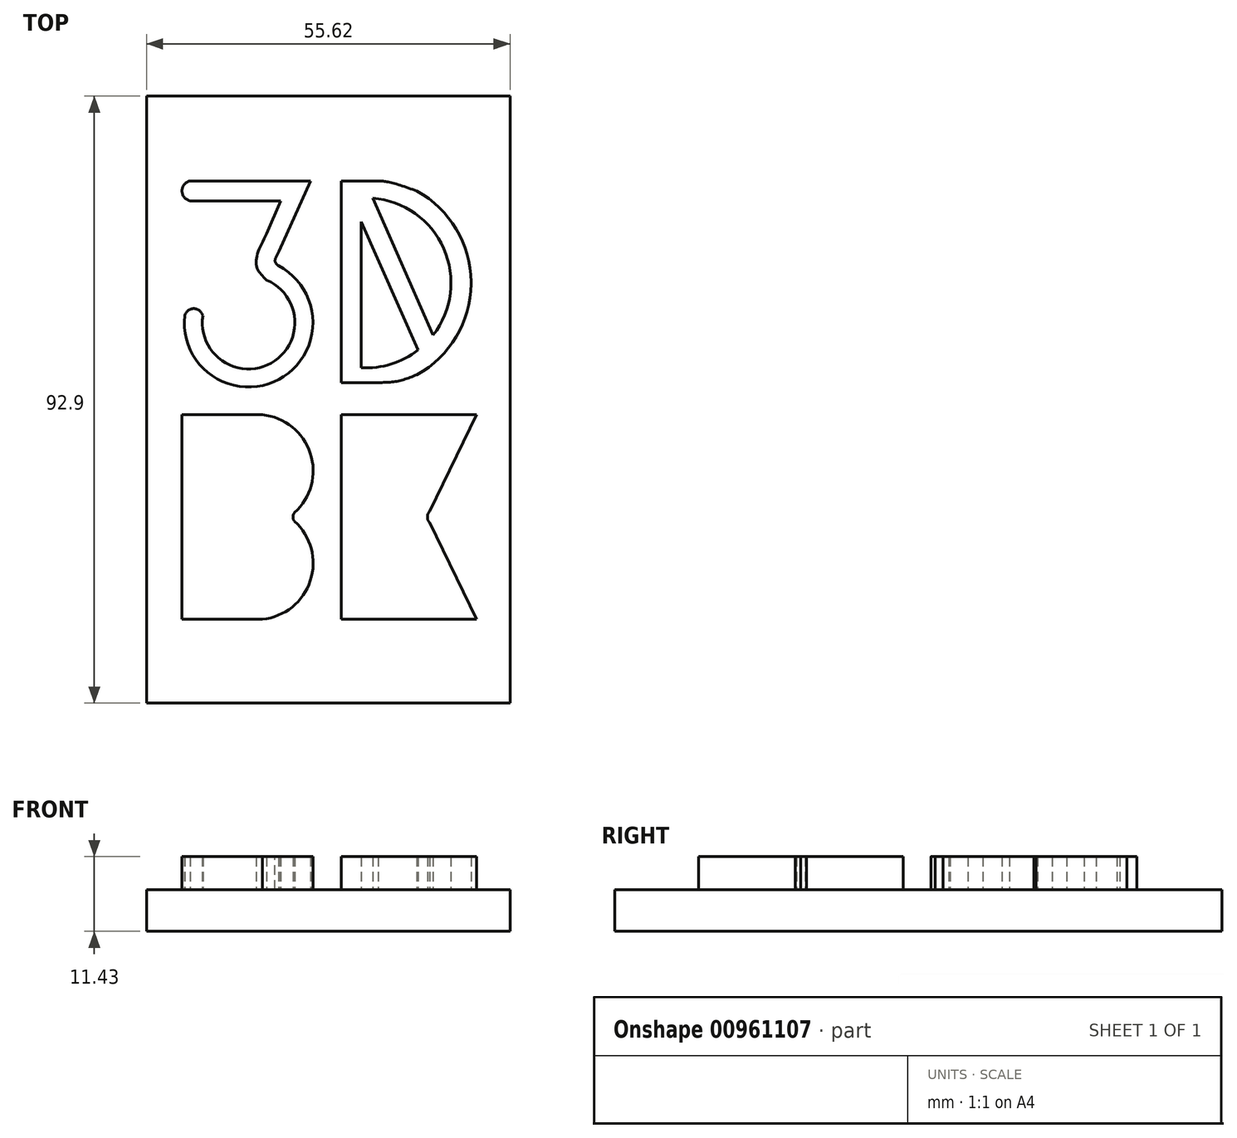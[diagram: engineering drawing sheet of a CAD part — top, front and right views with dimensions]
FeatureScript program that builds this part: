
annotation { "Feature Type Name" : "Feature", "Feature Type Description" : "" }
export const myFeature = defineFeature(function(context is Context, id is Id, definition is map)
    precondition{}
    {
        {
            var Q0;
            Q0=qCreatedBy(makeId("Top.planeOp"),FACE);
            var sketch = newSketch(context, id + "F0", { "sketchPlane" : qUnion([Q0])});
            skLineSegment(sketch, "E0", {"start": v(0, 56.35) * mm, "end": v(0, -56.35) * mm});
            skLineSegment(sketch, "E1", {"start": v(56.35, 0) * mm, "end": v(-56.35, 0) * mm});
            skPoint(sketch, "E2", {"position": v(0, 0) * mm});
            skPoint(sketch, "E3", {"position": v(-22.39, -33.62) * mm});
            skPoint(sketch, "E4", {"position": v(-22.39, 33.48) * mm});
            skPoint(sketch, "E5", {"position": v(21.85, 33.48) * mm});
            skLineSegment(sketch, "E6", {"start": v(1.95, 33.48) * mm, "end": v(7.67, 33.48) * mm});
            skLineSegment(sketch, "E7", {"start": v(21.85, -33.62) * mm, "end": v(1.95, -33.62) * mm});
            skLineSegment(sketch, "E8", {"start": v(21.85, 18.05) * mm, "end": v(21.85, 17.68) * mm});
            skLineSegment(sketch, "E9", {"start": v(-2.74, 33.48) * mm, "end": v(-21.16, 33.48) * mm});
            skLineSegment(sketch, "E10", {"start": v(-22.39, -33.62) * mm, "end": v(-10.07, -33.62) * mm});
            skLineSegment(sketch, "E11", {"start": v(-22.39, -2.3) * mm, "end": v(-22.39, -33.62) * mm});
            skPoint(sketch, "E12", {"position": v(-22.39, 31.95) * mm});
            skPoint(sketch, "E12.positionSnap0", {"position": v(-21.16, 31.95) * mm});
            skArc(sketch, "E13", {"start": v(-21.16, 33.48) * mm, "mid": v(-22.39, 31.95) * mm, "end": v(-21.16, 30.43) * mm});
            skPoint(sketch, "E14", {"position": v(-2.74, 33.48) * mm});
            skPoint(sketch, "E15", {"position": v(-7.3, 30.43) * mm});
            skLineSegment(sketch, "E16", {"start": v(-21.16, 30.43) * mm, "end": v(-7.3, 30.43) * mm});
            skPoint(sketch, "E17", {"position": v(-11.04, 20.68) * mm});
            skPoint(sketch, "E18", {"position": v(-9.45, 18.3) * mm});
            skPoint(sketch, "E19", {"position": v(-9.45, 25.39) * mm});
            skFitSpline(sketch, "E20", {"points": [v(-9.45, 25.39) * mm, v(-11.04, 20.68) * mm, v(-9.45, 18.3) * mm], "startDerivative": vector(-4.65, -9.06) * mm, "endDerivative": vector(5.1, -4.94) * mm});
            skLineSegment(sketch, "E21", {"start": v(-7.3, 30.43) * mm, "end": v(-9.45, 25.39) * mm});
            skPoint(sketch, "E22", {"position": v(-19.2, 12.85) * mm});
            skPoint(sketch, "E23", {"position": v(-12.14, 4.7) * mm});
            skArc(sketch, "E24", {"start": v(-19.2, 12.85) * mm, "mid": v(-8.74, 5.6) * mm, "end": v(-9.45, 18.3) * mm});
            skPoint(sketch, "E25", {"position": v(-8.14, 21.15) * mm});
            skPoint(sketch, "E26", {"position": v(-7.55, 20.43) * mm});
            skPoint(sketch, "E27", {"position": v(-7.55, 22.7) * mm});
            skFitSpline(sketch, "E28", {"points": [v(-7.55, 22.7) * mm, v(-8.14, 21.15) * mm, v(-7.55, 20.43) * mm], "startDerivative": vector(-1.74, -3) * mm, "endDerivative": vector(1.9, -1.47) * mm});
            skLineSegment(sketch, "E29", {"start": v(-2.74, 33.48) * mm, "end": v(-7.55, 22.7) * mm});
            skArc(sketch, "E30.0", {"start": v(-21.98, 12.85) * mm, "mid": v(-7.57, 3.08) * mm, "end": v(-7.62, 20.5) * mm});
            skPoint(sketch, "E31", {"position": v(-21.98, 12.85) * mm});
            skPoint(sketch, "E32", {"position": v(-20.63, 13.93) * mm});
            skArc(sketch, "E33", {"start": v(-19.2, 12.85) * mm, "mid": v(-20.59, 13.94) * mm, "end": v(-21.98, 12.85) * mm});
            skLineSegment(sketch, "E34", {"start": v(1.95, 33.48) * mm, "end": v(1.95, 2.25) * mm});
            skPoint(sketch, "E35", {"position": v(21.85, 18.05) * mm});
            skArc(sketch, "E36", {"start": v(13.56, 3.8) * mm, "mid": v(21.85, 17.87) * mm, "end": v(13.56, 31.93) * mm});
            skPoint(sketch, "E37", {"position": v(7.67, 33.48) * mm});
            skPoint(sketch, "E38", {"position": v(13.56, 31.93) * mm});
            skPoint(sketch, "E39", {"position": v(13.56, 3.8) * mm});
            skArc(sketch, "E40.0", {"start": v(5.03, 4.88) * mm, "mid": v(9.62, 5.44) * mm, "end": v(13.73, 7.58) * mm});
            skLineSegment(sketch, "E40.1", {"start": v(5.03, 27.26) * mm, "end": v(5.03, 4.88) * mm});
            skLineSegment(sketch, "E41", {"start": v(5.03, 27.26) * mm, "end": v(13.73, 7.58) * mm});
            skLineSegment(sketch, "E42", {"start": v(16.04, 9.89) * mm, "end": v(6.78, 30.83) * mm});
            skLineSegment(sketch, "E43", {"start": v(-22.39, -2.3) * mm, "end": v(-10.07, -2.3) * mm});
            skLineSegment(sketch, "E44", {"start": v(1.95, -2.3) * mm, "end": v(1.95, -33.62) * mm});
            skLineSegment(sketch, "E45", {"start": v(1.95, -2.3) * mm, "end": v(22.67, -2.3) * mm});
            skLineSegment(sketch, "E46", {"start": v(22.67, -2.3) * mm, "end": v(15.49, -17.1) * mm});
            skFitSpline(sketch, "E47", {"points": [v(15.49, -17.1) * mm, v(15.2, -17.6) * mm, v(15.17, -17.96) * mm], "startDerivative": vector(-0.63, -0.9) * mm, "endDerivative": vector(0.03, -0.82) * mm});
            skLineSegment(sketch, "E48.MirrorCS", {"start": v(1.95, -33.62) * mm, "end": v(22.67, -33.62) * mm});
            skLineSegment(sketch, "E49.MirrorCS", {"start": v(22.67, -33.62) * mm, "end": v(15.49, -18.82) * mm});
            skFitSpline(sketch, "E50.MirrorCS", {"points": [v(15.49, -18.82) * mm, v(15.2, -18.34) * mm, v(15.17, -17.96) * mm], "startDerivative": vector(-0.63, 0.9) * mm, "endDerivative": vector(0.03, 0.82) * mm});
            skArc(sketch, "E51", {"start": v(-5.17, -17.31) * mm, "mid": v(-2.75, -8.22) * mm, "end": v(-10.07, -2.3) * mm});
            skFitSpline(sketch, "E52", {"points": [v(-5.17, -17.31) * mm, v(-5.38, -17.68) * mm, v(-5.4, -17.96) * mm], "startDerivative": vector(-0.48, -0.68) * mm, "endDerivative": vector(0.02, -0.62) * mm});
            skArc(sketch, "E53.MirrorCS", {"start": v(-5.17, -18.61) * mm, "mid": v(-2.75, -27.7) * mm, "end": v(-10.07, -33.62) * mm});
            skFitSpline(sketch, "E54.MirrorCS", {"points": [v(-5.17, -18.61) * mm, v(-5.38, -18.25) * mm, v(-5.4, -17.96) * mm], "startDerivative": vector(-0.48, 0.68) * mm, "endDerivative": vector(0.02, 0.62) * mm});
            skPoint(sketch, "E55.end.orphan", {"position": v(-10.07, -33.62) * mm});
            skPoint(sketch, "E56.orphan", {"position": v(-10.07, -17.96) * mm});
            skPoint(sketch, "E57.orphan", {"position": v(0, -33.62) * mm});
            skLineSegment(sketch, "E58.MirrorCS", {"start": v(0, 2.62) * mm, "end": v(7.67, 2.62) * mm});
            skArc(sketch, "E59.trimOffspring", {"start": v(16.04, 9.89) * mm, "mid": v(17.67, 23.12) * mm, "end": v(6.78, 30.83) * mm});
            skPoint(sketch, "E60", {"position": v(7.67, 2.62) * mm});
            skFitSpline(sketch, "E61", {"points": [v(13.56, 3.8) * mm, v(10.55, 2.81) * mm, v(7.67, 2.62) * mm], "startDerivative": vector(-5.9, -2.33) * mm, "endDerivative": vector(-5.9, -0.02) * mm});
            skPoint(sketch, "E62.1.internal.snap0", {"position": v(9.38, 17.42) * mm});
            skFitSpline(sketch, "E62", {"points": [v(13.56, 31.93) * mm, v(9.38, 33.27) * mm, v(7.67, 33.48) * mm], "startDerivative": vector(-7.54, 2.7) * mm, "endDerivative": vector(-3.99, 0.22) * mm});
            skPoint(sketch, "E63.orphan", {"position": v(10.87, 2.62) * mm});
            skPoint(sketch, "E64.orphan", {"position": v(0, 33.48) * mm});
            skPoint(sketch, "E65.trimOffspring.start.orphan", {"position": v(21.85, 2.62) * mm});
            skLineSegment(sketch, "E66", {"start": v(-27.8, 0) * mm, "end": v(-27.8, 46.45) * mm});
            skLineSegment(sketch, "E67", {"start": v(-27.8, 46.45) * mm, "end": v(0, 46.45) * mm});
            skLineSegment(sketch, "E68.MirrorCS", {"start": v(27.8, 0) * mm, "end": v(27.8, 46.45) * mm});
            skLineSegment(sketch, "E69.MirrorCS", {"start": v(-27.8, -46.45) * mm, "end": v(0, -46.45) * mm});
            skLineSegment(sketch, "E70.MirrorCS", {"start": v(-27.8, 0) * mm, "end": v(-27.8, -46.45) * mm});
            skLineSegment(sketch, "E71.MirrorCS", {"start": v(27.8, 46.45) * mm, "end": v(0, 46.45) * mm});
            skLineSegment(sketch, "E72.MirrorCS", {"start": v(27.8, 0) * mm, "end": v(27.8, -46.45) * mm});
            skLineSegment(sketch, "E73.MirrorCS", {"start": v(27.8, -46.45) * mm, "end": v(0, -46.45) * mm});
            skSolve(sketch);
        }
        {
            var Q0;
            Q0=qCreatedBy(makeId("Top.planeOp"),FACE);
            var sketch = newSketch(context, id + "F1", { "sketchPlane" : qUnion([Q0])});
            skLineSegment(sketch, "E74.bottom", {"start": v(-27.8, 46.45) * mm, "end": v(27.8, 46.45) * mm});
            skLineSegment(sketch, "E74.top", {"start": v(-27.8, -46.45) * mm, "end": v(27.8, -46.45) * mm});
            skLineSegment(sketch, "E74.left", {"start": v(-27.8, 46.45) * mm, "end": v(-27.8, -46.45) * mm});
            skLineSegment(sketch, "E74.right", {"start": v(27.8, 46.45) * mm, "end": v(27.8, -46.45) * mm});
            skSolve(sketch);
        }
        {
            var Q0;
            Q0=makeQuery(id+"F1.imprint","IMPRINT",FACE,{"disambiguationData":[TD([[makeQuery(id+"F1.imprint","IMPRINT",EDGE,{"derivedFrom":sQuery(id+"F1.wireOp",EDGE,"E74.bottom")}),-1.0]])]});
            extrude(context, id + "F2", {"entities" : qUnion([Q0]), "oppositeDirection" : true, "depth" : 6.35 * mm, "offsetDistance" : 25.4 * mm});
        }
        {
            var Q0;
            {var subQ7=sQuery(id+"F0.wireOp",EDGE,"E6");Q0=makeQuery(id+"F0.imprint","IMPRINT",FACE,{"disambiguationData":[TD([[makeQuery(id+"F0.imprint","IMPRINT",EDGE,{"derivedFrom":subQ7}),-1.0]])]});}
            var Q1;
            Q1=makeQuery(id+"F0.imprint","IMPRINT",FACE,{"disambiguationData":[TD([[makeQuery(id+"F0.imprint","IMPRINT",EDGE,{"derivedFrom":sQuery(id+"F0.wireOp",EDGE,"E9")}),1.0]])]});
            var Q2;
            {var subQ0=sQuery(id+"F0.wireOp",EDGE,"E44");Q2=makeQuery(id+"F0.imprint","IMPRINT",FACE,{"disambiguationData":[TD([[makeQuery(id+"F0.imprint","IMPRINT",EDGE,{"derivedFrom":subQ0}),1.0]])]});}
            var Q3;
            Q3=makeQuery(id+"F0.imprint","IMPRINT",FACE,{"disambiguationData":[TD([[makeQuery(id+"F0.imprint","IMPRINT",EDGE,{"derivedFrom":sQuery(id+"F0.wireOp",EDGE,"E10")}),1.0]])]});
            extrude(context, id + "F3", {"entities" : qUnion([Q0, Q1, Q2, Q3]), "operationType" : NewBodyOperationType.ADD, "depth" : 5.08 * mm, "offsetDistance" : 25.4 * mm});
        }
    });
